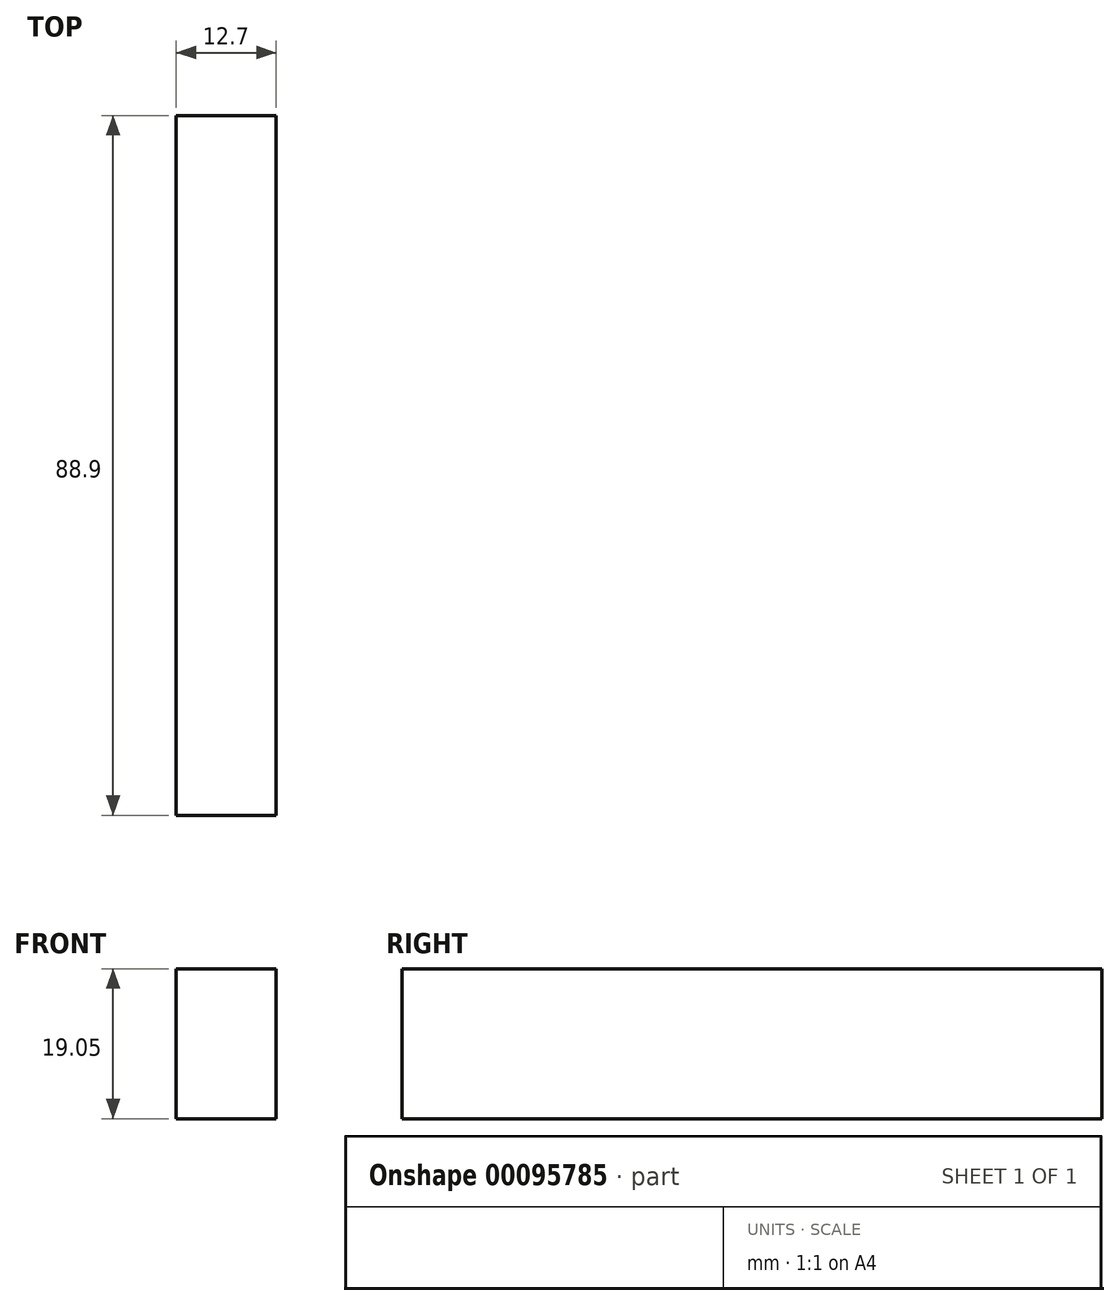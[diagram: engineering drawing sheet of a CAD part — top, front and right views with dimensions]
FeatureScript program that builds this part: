
annotation { "Feature Type Name" : "Feature", "Feature Type Description" : "" }
export const myFeature = defineFeature(function(context is Context, id is Id, definition is map)
    precondition{}
    {
        {
            var Q0;
            Q0=qCreatedBy(makeId("Front.planeOp"),FACE);
            var sketch = newSketch(context, id + "F0", { "sketchPlane" : qUnion([Q0])});
            skLineSegment(sketch, "E0.bottom", {"start": v(-2.45, 0.38) * mm, "end": v(-15.15, 0.38) * mm});
            skLineSegment(sketch, "E0.top", {"start": v(-2.45, 19.43) * mm, "end": v(-15.15, 19.43) * mm});
            skLineSegment(sketch, "E0.left", {"start": v(-2.45, 0.38) * mm, "end": v(-2.45, 19.43) * mm});
            skLineSegment(sketch, "E0.right", {"start": v(-15.15, 0.38) * mm, "end": v(-15.15, 19.43) * mm});
            skPoint(sketch, "E0.middle", {"position": v(-8.8, 9.9) * mm});
            skSolve(sketch);
        }
        {
            var Q0;
            Q0=makeQuery(id+"F0.imprint","IMPRINT",FACE,{"disambiguationData":[TD([[makeQuery(id+"F0.imprint","IMPRINT",EDGE,{"derivedFrom":sQuery(id+"F0.wireOp",EDGE,"E0.bottom")}),-1.0]])]});
            extrude(context, id + "F1", {"entities" : qUnion([Q0]), "endBound" : BoundingType.SYMMETRIC, "depth" : 88.9 * mm});
        }
    });
